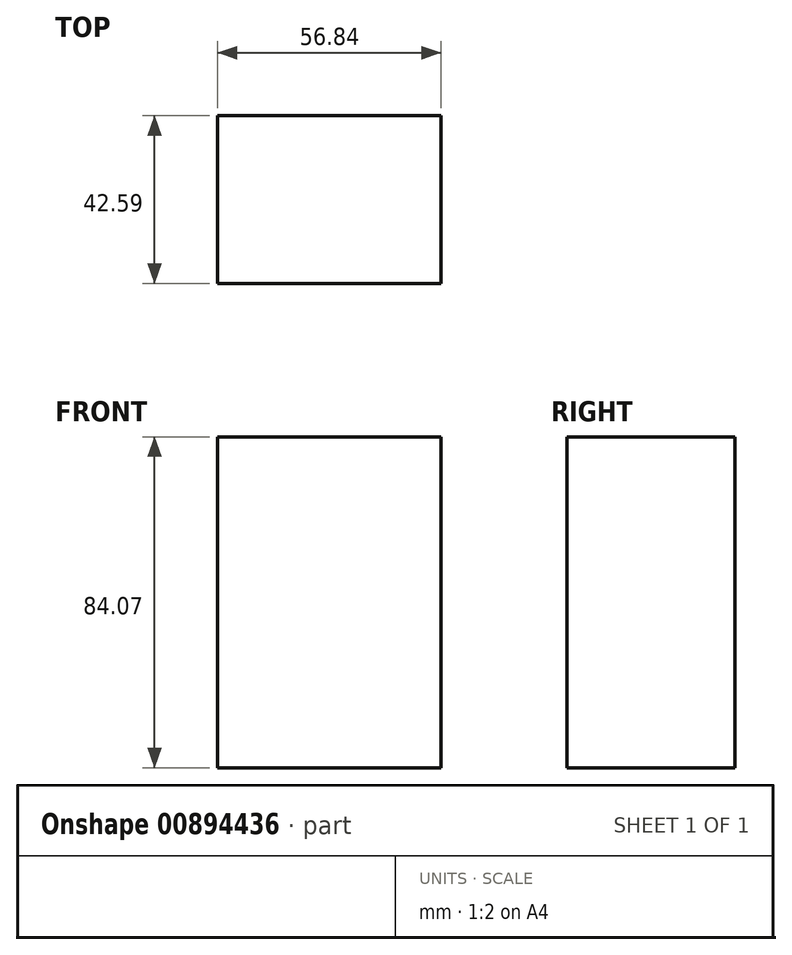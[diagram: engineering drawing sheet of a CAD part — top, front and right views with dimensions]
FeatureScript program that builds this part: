
annotation { "Feature Type Name" : "Feature", "Feature Type Description" : "" }
export const myFeature = defineFeature(function(context is Context, id is Id, definition is map)
    precondition{}
    {
        {
            var Q0;
            Q0=qCreatedBy(makeId("Top.planeOp"),FACE);
            var sketch = newSketch(context, id + "F0", { "sketchPlane" : qUnion([Q0])});
            skLineSegment(sketch, "E0.bottom", {"start": v(-41.65, -17.75) * mm, "end": v(15.19, -17.75) * mm});
            skLineSegment(sketch, "E0.top", {"start": v(-41.65, 24.84) * mm, "end": v(15.19, 24.84) * mm});
            skLineSegment(sketch, "E0.left", {"start": v(-41.65, -17.75) * mm, "end": v(-41.65, 24.84) * mm});
            skLineSegment(sketch, "E0.right", {"start": v(15.19, -17.75) * mm, "end": v(15.19, 24.84) * mm});
            skSolve(sketch);
        }
        {
            var Q0;
            Q0 = qSketchRegion(id + "F0", true);
            extrude(context, id + "F1", {"entities" : qUnion([Q0]), "depth" : 84.07 * mm, "offsetDistance" : 25.4 * mm});
        }
    });
